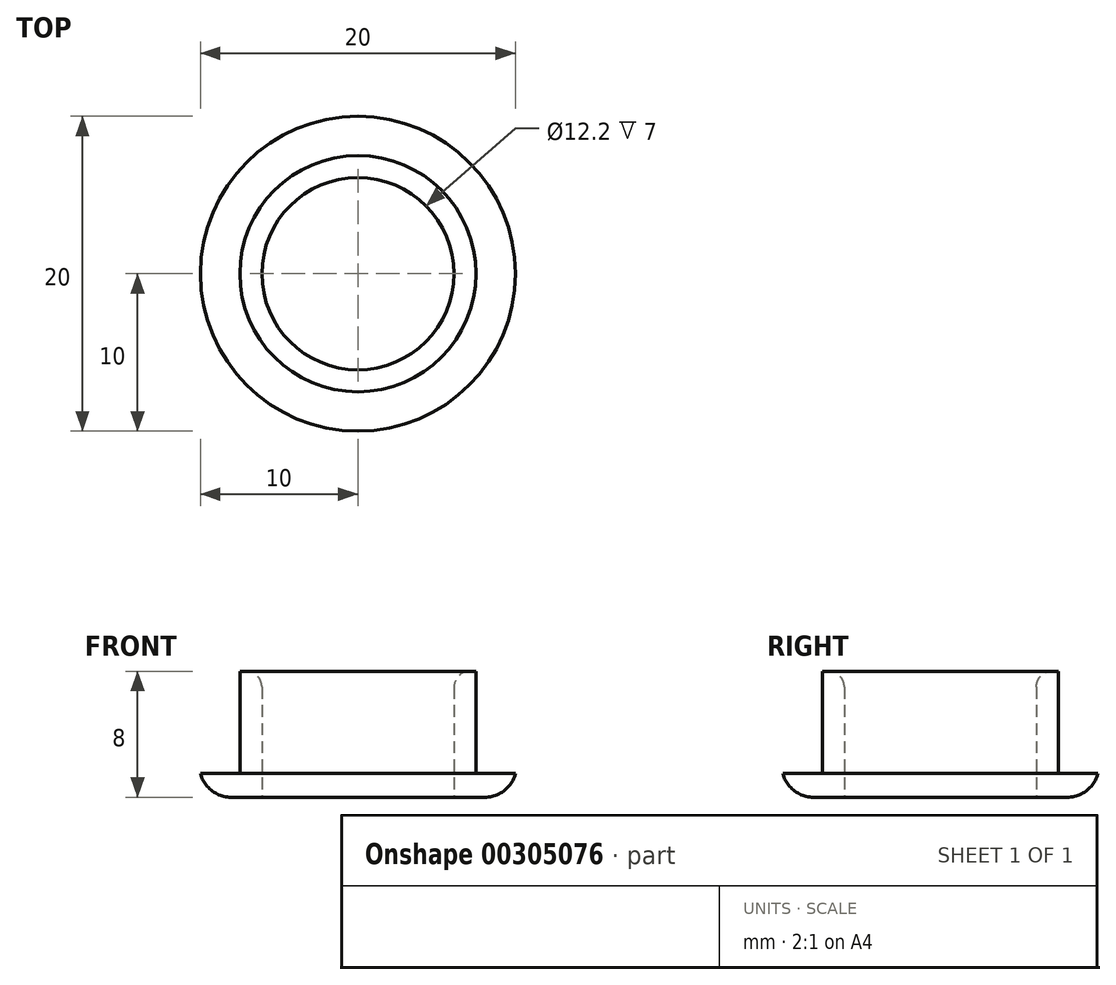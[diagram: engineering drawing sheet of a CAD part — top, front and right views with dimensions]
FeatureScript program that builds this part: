
annotation { "Feature Type Name" : "Feature", "Feature Type Description" : "" }
export const myFeature = defineFeature(function(context is Context, id is Id, definition is map)
    precondition{}
    {
        {
            var Q0;
            Q0=qCreatedBy(makeId("Top.planeOp"),FACE);
            var sketch = newSketch(context, id + "F0", { "sketchPlane" : qUnion([Q0])});
            skCircle(sketch, "E0", {"center": v(0, 0) * mm, "radius": 6.1 * mm});
            skCircle(sketch, "E1", {"center": v(0, 0) * mm, "radius": 10 * mm});
            skCircle(sketch, "E2", {"center": v(0, 0) * mm, "radius": 7.5 * mm});
            skSolve(sketch);
        }
        {
            var Q0;
            Q0=makeQuery(id+"F0.imprint","IMPRINT",FACE,{"disambiguationData":[TD([[makeQuery(id+"F0.imprint","IMPRINT",EDGE,{"derivedFrom":sQuery(id+"F0.wireOp",EDGE,"E1")}),1.0]])]});
            extrude(context, id + "F1", {"entities" : qUnion([Q0]), "offsetDistance" : 25 * mm, "depth" : 1.5 * mm});
        }
        {
            var Q0;
            Q0=makeQuery(id+"F0.imprint","IMPRINT",FACE,{"disambiguationData":[TD([[makeQuery(id+"F0.imprint","IMPRINT",EDGE,{"derivedFrom":sQuery(id+"F0.wireOp",EDGE,"E0")}),-1.0]])]});
            extrude(context, id + "F2", {"entities" : qUnion([Q0]), "operationType" : NewBodyOperationType.ADD, "offsetDistance" : 25 * mm, "depth" : 8 * mm});
        }
        {
            var Q0;
            Q0=makeQuery(id+"F1.opExtrude","CAP_EDGE",EDGE,{"disambiguationData":[OSD([sQuery(id+"F0.wireOp",EDGE,"E1")])],"isStart":true});
            fillet(context, id + "F3", {"entities" : qUnion([Q0]), "radius" : 2 * mm, "tangentPropagation" : true, "allowEdgeOverflow" : false});
        }
        {
            var Q0;
            Q0=makeQuery(id+"F2.opExtrude","CAP_EDGE",EDGE,{"disambiguationData":[OSD([sQuery(id+"F0.wireOp",EDGE,"E0")])],"isStart":false});
            fillet(context, id + "F4", {"entities" : qUnion([Q0]), "radius" : 1 * mm, "tangentPropagation" : true, "allowEdgeOverflow" : false});
        }
    });
